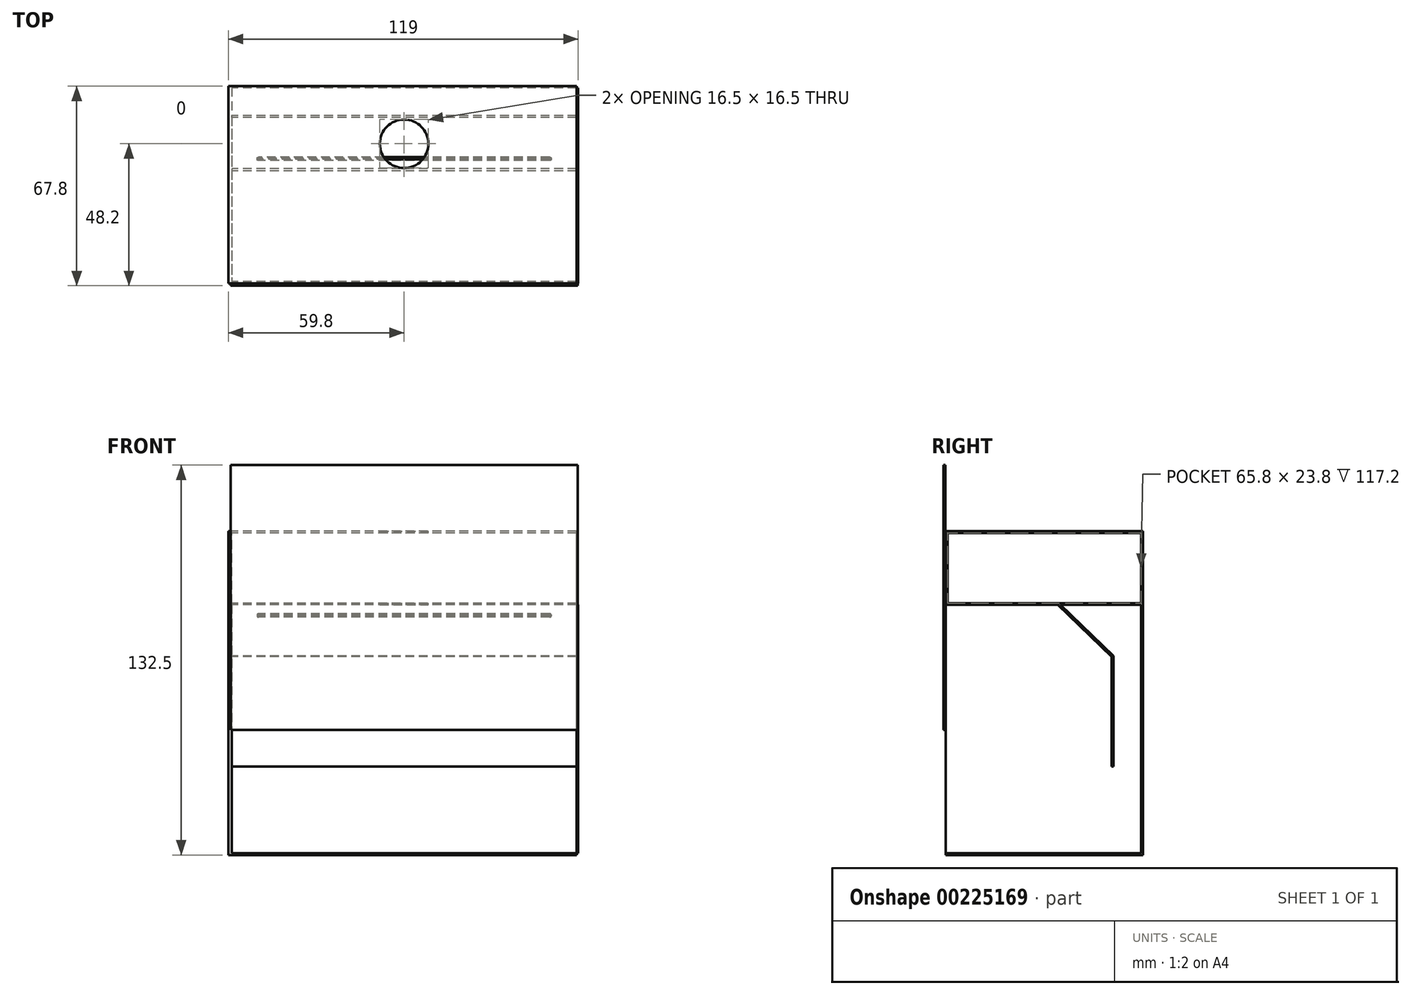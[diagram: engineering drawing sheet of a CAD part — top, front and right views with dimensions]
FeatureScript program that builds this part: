
annotation { "Feature Type Name" : "Feature", "Feature Type Description" : "" }
export const myFeature = defineFeature(function(context is Context, id is Id, definition is map)
    precondition{}
    {
        {
            var Q0;
            Q0=qCreatedBy(makeId("Right.planeOp"),FACE);
            var sketch = newSketch(context, id + "F0", { "sketchPlane" : qUnion([Q0])});
            skLineSegment(sketch, "E0.bottom", {"start": v(33.5, -42.5) * mm, "end": v(-33.5, -42.5) * mm});
            skLineSegment(sketch, "E0.top", {"start": v(32.9, 42.5) * mm, "end": v(-33.5, 42.5) * mm});
            skLineSegment(sketch, "E0.left", {"start": v(33.5, -42.5) * mm, "end": v(33.5, 42.5) * mm});
            skLineSegment(sketch, "E0.right", {"start": v(-33.5, -42.5) * mm, "end": v(-33.5, -41.9) * mm});
            skPoint(sketch, "E0.middle", {"position": v(0, 0) * mm});
            skLineSegment(sketch, "E1", {"start": v(23.5, -12.5) * mm, "end": v(23.5, 25.15) * mm});
            skLineSegment(sketch, "E2", {"start": v(23.5, 25.15) * mm, "end": v(5.5, 42.5) * mm});
            skLineSegment(sketch, "E3.1", {"start": v(32.9, -41.9) * mm, "end": v(-32.9, -41.9) * mm});
            skLineSegment(sketch, "E3.2", {"start": v(32.9, -41.9) * mm, "end": v(32.9, 42.5) * mm});
            skLineSegment(sketch, "E3.3", {"start": v(32.9, 43.1) * mm, "end": v(-32.9, 43.1) * mm});
            skPoint(sketch, "E4.orphan", {"position": v(5.5, 42.5) * mm});
            skLineSegment(sketch, "E5.0", {"start": v(22.9, 24.9) * mm, "end": v(10.54, 36.8) * mm});
            skLineSegment(sketch, "E5.1", {"start": v(22.9, -12.5) * mm, "end": v(22.9, 24.9) * mm});
            skLineSegment(sketch, "E6", {"start": v(10.54, 36.8) * mm, "end": v(4.64, 42.5) * mm});
            skLineSegment(sketch, "E7", {"start": v(22.9, -12.5) * mm, "end": v(23.5, -12.5) * mm});
            skLineSegment(sketch, "E8", {"start": v(-32.9, -41.9) * mm, "end": v(-33.5, -41.9) * mm});
            skLineSegment(sketch, "E9.trimOffspring", {"start": v(-33.5, 42.5) * mm, "end": v(-33.5, 43.1) * mm});
            skLineSegment(sketch, "E10.bottom", {"start": v(-33.5, 42.5) * mm, "end": v(32.9, 42.5) * mm});
            skLineSegment(sketch, "E10.top", {"start": v(-33.5, -42.5) * mm, "end": v(33.5, -42.5) * mm});
            skLineSegment(sketch, "E10.left", {"start": v(-33.5, 42.5) * mm, "end": v(-33.5, -42.5) * mm});
            skLineSegment(sketch, "E10.right", {"start": v(33.5, 42.5) * mm, "end": v(33.5, -42.5) * mm});
            skLineSegment(sketch, "E11.top", {"start": v(-33.5, 67.5) * mm, "end": v(33.5, 67.5) * mm});
            skLineSegment(sketch, "E11.left", {"start": v(-33.5, 42.5) * mm, "end": v(-33.5, 67.5) * mm});
            skLineSegment(sketch, "E11.right", {"start": v(33.5, 42.5) * mm, "end": v(33.5, 67.5) * mm});
            skLineSegment(sketch, "E12.0", {"start": v(32.9, 43.1) * mm, "end": v(32.9, 66.9) * mm});
            skLineSegment(sketch, "E12.1", {"start": v(-32.9, 66.9) * mm, "end": v(32.9, 66.9) * mm});
            skLineSegment(sketch, "E12.2", {"start": v(-32.9, 43.1) * mm, "end": v(-32.9, 66.9) * mm});
            skSolve(sketch);
        }
        {
            var Q0;
            Q0=makeQuery(id+"F0.imprint","IMPRINT",FACE,{"disambiguationData":[TD([[makeQuery(id+"F0.imprint","IMPRINT",EDGE,{"derivedFrom":sQuery(id+"F0.wireOp",EDGE,"E1")}),1.0]])]});
            var Q1;
            {var subQ1=sQuery(id+"F0.wireOp",EDGE,"tK16oM9A-ym4e-ytda-ZOBi-XifHDms7LfMU");Q1=makeQuery(id+"F0.imprint","IMPRINT",FACE,{"disambiguationData":[TD([[makeQuery(id+"F0.imprint","IMPRINT",EDGE,{"derivedFrom":subQ1}),-1.0]])]});}
            var Q2;
            Q2=makeQuery(id+"F0.imprint","IMPRINT",FACE,{"disambiguationData":[TD([[makeQuery(id+"F0.imprint","IMPRINT",EDGE,{"derivedFrom":sQuery(id+"F0.wireOp",EDGE,"E3.1")}),1.0]])]});
            extrude(context, id + "F1", {"entities" : qUnion([Q0, Q1, Q2]), "depth" : 118.4 * mm});
        }
        {
            var Q0;
            Q0=makeQuery(id+"F0.imprint","IMPRINT",FACE,{"disambiguationData":[TD([[makeQuery(id+"F0.imprint","IMPRINT",EDGE,{"derivedFrom":sQuery(id+"F0.wireOp",EDGE,"E1")}),-1.0]])]});
            var Q1;
            {var subQ0=sQuery(id+"F0.wireOp",EDGE,"E12.0");Q1=makeQuery(id+"F0.imprint","IMPRINT",FACE,{"disambiguationData":[TD([[makeQuery(id+"F0.imprint","IMPRINT",EDGE,{"derivedFrom":subQ0}),1.0]])]});}
            var Q2;
            {var subQ5=sQuery(id+"F0.wireOp",EDGE,"E3.3");Q2=makeQuery(id+"F0.imprint","IMPRINT",FACE,{"disambiguationData":[TD([[makeQuery(id+"F0.imprint","IMPRINT",EDGE,{"derivedFrom":subQ5}),1.0]])]});}
            var Q3;
            Q3=makeQuery(id+"F0.imprint","IMPRINT",FACE,{"disambiguationData":[TD([[makeQuery(id+"F0.imprint","IMPRINT",EDGE,{"derivedFrom":sQuery(id+"F0.wireOp",EDGE,"E1")}),1.0]])]});
            var Q4;
            Q4=makeQuery(id+"F0.imprint","IMPRINT",FACE,{"disambiguationData":[TD([[makeQuery(id+"F0.imprint","IMPRINT",EDGE,{"derivedFrom":sQuery(id+"F0.wireOp",EDGE,"E3.1")}),1.0]])]});
            var Q5;
            {var subQ1=sQuery(id+"F0.wireOp",EDGE,"tK16oM9A-ym4e-ytda-ZOBi-XifHDms7LfMU");Q5=makeQuery(id+"F0.imprint","IMPRINT",FACE,{"disambiguationData":[TD([[makeQuery(id+"F0.imprint","IMPRINT",EDGE,{"derivedFrom":subQ1}),-1.0]])]});}
            extrude(context, id + "F2", {"entities" : qUnion([Q0, Q1, Q2, Q3, Q4, Q5]), "depth" : 0.6 * mm});
        }
        {
            var Q0;
            Q0=makeQuery(id+"F1.opExtrude","CAP_FACE",FACE,{"disambiguationData":[OSD([sQuery(id+"F0.wireOp",EDGE,"E1"),sQuery(id+"F0.wireOp",EDGE,"E2"),sQuery(id+"F0.wireOp",EDGE,"E3.1"),sQuery(id+"F0.wireOp",EDGE,"E3.2"),sQuery(id+"F0.wireOp",EDGE,"E3.3"),sQuery(id+"F0.wireOp",EDGE,"E5.0"),sQuery(id+"F0.wireOp",EDGE,"E5.1"),sQuery(id+"F0.wireOp",EDGE,"E6"),sQuery(id+"F0.wireOp",EDGE,"E7"),sQuery(id+"F0.wireOp",EDGE,"tK16oM9A-ym4e-ytda-ZOBi-XifHDms7LfMU"),sQuery(id+"F0.wireOp",EDGE,"E8"),sQuery(id+"F0.wireOp",EDGE,"E10.bottom"),sQuery(id+"F0.wireOp",EDGE,"E10.top"),sQuery(id+"F0.wireOp",EDGE,"E10.left"),sQuery(id+"F0.wireOp",EDGE,"E10.right")])],"isStart":false});
            var sketch = newSketch(context, id + "F3", { "sketchPlane" : qUnion([Q0])});
            skLineSegment(sketch, "E13.bottom", {"start": v(33.5, -42.5) * mm, "end": v(-33.5, -42.5) * mm});
            skLineSegment(sketch, "E13.left", {"start": v(33.5, -42.5) * mm, "end": v(33.5, 42.5) * mm});
            skLineSegment(sketch, "E13.right", {"start": v(-33.5, -42.5) * mm, "end": v(-33.5, 42.5) * mm});
            skLineSegment(sketch, "E14.top", {"start": v(-33.5, 67.5) * mm, "end": v(33.5, 67.5) * mm});
            skLineSegment(sketch, "E14.left", {"start": v(-33.5, 42.5) * mm, "end": v(-33.5, 67.5) * mm});
            skLineSegment(sketch, "E14.right", {"start": v(33.5, 42.5) * mm, "end": v(33.5, 67.5) * mm});
            skSolve(sketch);
        }
        {
            var Q0;
            {var subQ3=sQuery(id+"F3.wireOp",EDGE,"E13.bottom");Q0=makeQuery(id+"F3.imprint","IMPRINT",FACE,{"disambiguationData":[TD([[makeQuery(id+"F3.imprint","IMPRINT",EDGE,{"derivedFrom":subQ3}),1.0]])]});}
            var Q1;
            Q1=makeQuery(id+"F0.imprint","IMPRINT",FACE,{"disambiguationData":[TD([[makeQuery(id+"F0.imprint","IMPRINT",EDGE,{"derivedFrom":sQuery(id+"F0.wireOp",EDGE,"E11.top")}),-1.0]])]});
            var Q2;
            Q2=makeQuery(id+"F3.imprint","IMPRINT",FACE,{"disambiguationData":[TD([[makeQuery(id+"F3.imprint","IMPRINT",EDGE,{"derivedFrom":makeQuery(id+"F1.opExtrude","CAP_EDGE",EDGE,{"disambiguationData":[OSD([sQuery(id+"F0.wireOp",EDGE,"E10.bottom")])],"isStart":false})}),1.0]])]});
            var Q3;
            Q3=makeQuery(id+"F3.imprint","IMPRINT",FACE,{"disambiguationData":[TD([[makeQuery(id+"F3.imprint","IMPRINT",EDGE,{"derivedFrom":makeQuery(id+"F1.opExtrude","CAP_EDGE",EDGE,{"disambiguationData":[OSD([sQuery(id+"F0.wireOp",EDGE,"E1")])],"isStart":false})}),-1.0]])]});
            var Q4;
            Q4=makeQuery(id+"F2.opExtrude","CAP_FACE",FACE,{"disambiguationData":[OSD([sQuery(id+"F0.wireOp",EDGE,"E10.top"),sQuery(id+"F0.wireOp",EDGE,"E10.left"),sQuery(id+"F0.wireOp",EDGE,"E10.right"),sQuery(id+"F0.wireOp",EDGE,"E11.top"),sQuery(id+"F0.wireOp",EDGE,"E11.left"),sQuery(id+"F0.wireOp",EDGE,"E11.right")])],"isStart":false});
            extrude(context, id + "F4", {"entities" : qUnion([Q0, Q1, Q2, Q3, Q4]), "operationType" : NewBodyOperationType.ADD, "depth" : 0.6 * mm});
        }
        {
            var Q0;
            Q0=makeQuery(id+"F1.opExtrude","SWEPT_FACE",FACE,{"disambiguationData":[OSD([sQuery(id+"F0.wireOp",EDGE,"E11.top")])]});
            var sketch = newSketch(context, id + "F5", { "sketchPlane" : qUnion([Q0])});
            skCircle(sketch, "E15", {"center": v(59.8, 13.9) * mm, "radius": 8.25 * mm});
            skPoint(sketch, "E15.centerSnap0", {"position": v(59.8, 32.9) * mm});
            skLineSegment(sketch, "E16", {"start": v(59.8, 32.9) * mm, "end": v(59.8, 13.9) * mm, "construction": true});
            skLineSegment(sketch, "E17.bottom", {"start": v(68.05, 13.9) * mm, "end": v(51.55, 13.9) * mm});
            skLineSegment(sketch, "E17.top", {"start": v(68.05, 32.9) * mm, "end": v(51.55, 32.9) * mm});
            skPoint(sketch, "E17.middle", {"position": v(59.8, 23.4) * mm});
            skSolve(sketch);
        }
        {
            var Q0;
            Q0=makeQuery(id+"F1.opExtrude","SWEPT_FACE",FACE,{"disambiguationData":[OSD([sQuery(id+"F0.wireOp",EDGE,"E5.0"),sQuery(id+"F0.wireOp",EDGE,"E6")])]});
            var sketch = newSketch(context, id + "F6", { "sketchPlane" : qUnion([Q0])});
            skLineSegment(sketch, "E18.bottom", {"start": v(109.3, 20.16) * mm, "end": v(10.3, 20.16) * mm});
            skLineSegment(sketch, "E18.top", {"start": v(109.3, 21.16) * mm, "end": v(10.3, 21.16) * mm});
            skLineSegment(sketch, "E18.left", {"start": v(109.8, 20.66) * mm, "end": v(109.8, 20.66) * mm});
            skLineSegment(sketch, "E18.right", {"start": v(9.8, 20.66) * mm, "end": v(9.8, 20.66) * mm});
            skPoint(sketch, "E18.middle", {"position": v(59.8, 20.66) * mm});
            skPoint(sketch, "E18.middle.positionSnap0", {"position": v(59.8, 31.03) * mm});
            skPoint(sketch, "E18.centerSnap0", {"position": v(59.8, 31.03) * mm});
            skPoint(sketch, "E19.visualSharp", {"position": v(9.8, 21.16) * mm});
            skArc(sketch, "E19.filletArc", {"start": v(10.3, 21.16) * mm, "mid": v(9.95, 21) * mm, "end": v(9.8, 20.66) * mm});
            skPoint(sketch, "E20.visualSharp", {"position": v(9.8, 20.16) * mm});
            skArc(sketch, "E20.filletArc", {"start": v(9.8, 20.66) * mm, "mid": v(9.95, 20.3) * mm, "end": v(10.3, 20.16) * mm});
            skPoint(sketch, "E21.visualSharp", {"position": v(109.8, 21.16) * mm});
            skArc(sketch, "E21.filletArc", {"start": v(109.8, 20.66) * mm, "mid": v(109.65, 21) * mm, "end": v(109.3, 21.16) * mm});
            skPoint(sketch, "E22.visualSharp", {"position": v(109.8, 20.16) * mm});
            skArc(sketch, "E22.filletArc", {"start": v(109.3, 20.16) * mm, "mid": v(109.65, 20.3) * mm, "end": v(109.8, 20.66) * mm});
            skSolve(sketch);
        }
        {
            var Q0;
            Q0=makeQuery(id+"F6.imprint","IMPRINT",FACE,{"disambiguationData":[TD([[makeQuery(id+"F6.imprint","IMPRINT",EDGE,{"derivedFrom":sQuery(id+"F6.wireOp",EDGE,"E18.bottom")}),-1.0]])]});
            extrude(context, id + "F7", {"entities" : qUnion([Q0]), "operationType" : NewBodyOperationType.REMOVE, "oppositeDirection" : true, "depth" : 1 * mm});
        }
        {
            var Q0;
            Q0=qCreatedBy(makeId("Top.planeOp"),FACE);
            var sketch = newSketch(context, id + "F8", { "sketchPlane" : qUnion([Q0])});
            skLineSegment(sketch, "E23.bottom", {"start": v(118.8, -34.3) * mm, "end": v(0.8, -34.3) * mm});
            skLineSegment(sketch, "E23.top", {"start": v(118.8, -33.7) * mm, "end": v(0.8, -33.7) * mm});
            skLineSegment(sketch, "E23.left", {"start": v(118.8, -34.3) * mm, "end": v(118.8, -33.7) * mm});
            skLineSegment(sketch, "E23.right", {"start": v(0.8, -34.3) * mm, "end": v(0.8, -33.7) * mm});
            skPoint(sketch, "E23.middle", {"position": v(59.8, -34) * mm});
            skSolve(sketch);
        }
        {
            var Q0;
            Q0=makeQuery(id+"F8.imprint","IMPRINT",FACE,{"disambiguationData":[TD([[makeQuery(id+"F8.imprint","IMPRINT",EDGE,{"derivedFrom":sQuery(id+"F8.wireOp",EDGE,"E23.bottom")}),-1.0]])]});
            extrude(context, id + "F9", {"entities" : qUnion([Q0]), "depth" : 90 * mm});
        }
        {
            var Q0;
            {var subQ0=sQuery(id+"F5.wireOp",EDGE,"E17.bottom");Q0=makeQuery(id+"F5.imprint","IMPRINT",FACE,{"disambiguationData":[TD([[makeQuery(id+"F5.imprint","IMPRINT",EDGE,{"derivedFrom":subQ0}),1.0]])]});}
            var Q1;
            {var subQ0=sQuery(id+"F5.wireOp",EDGE,"E17.bottom");Q1=makeQuery(id+"F5.imprint","IMPRINT",FACE,{"disambiguationData":[TD([[makeQuery(id+"F5.imprint","IMPRINT",EDGE,{"derivedFrom":subQ0}),-1.0]])]});}
            extrude(context, id + "F10", {"entities" : qUnion([Q0, Q1]), "operationType" : NewBodyOperationType.REMOVE, "oppositeDirection" : true, "depth" : 25 * mm});
        }
    });
